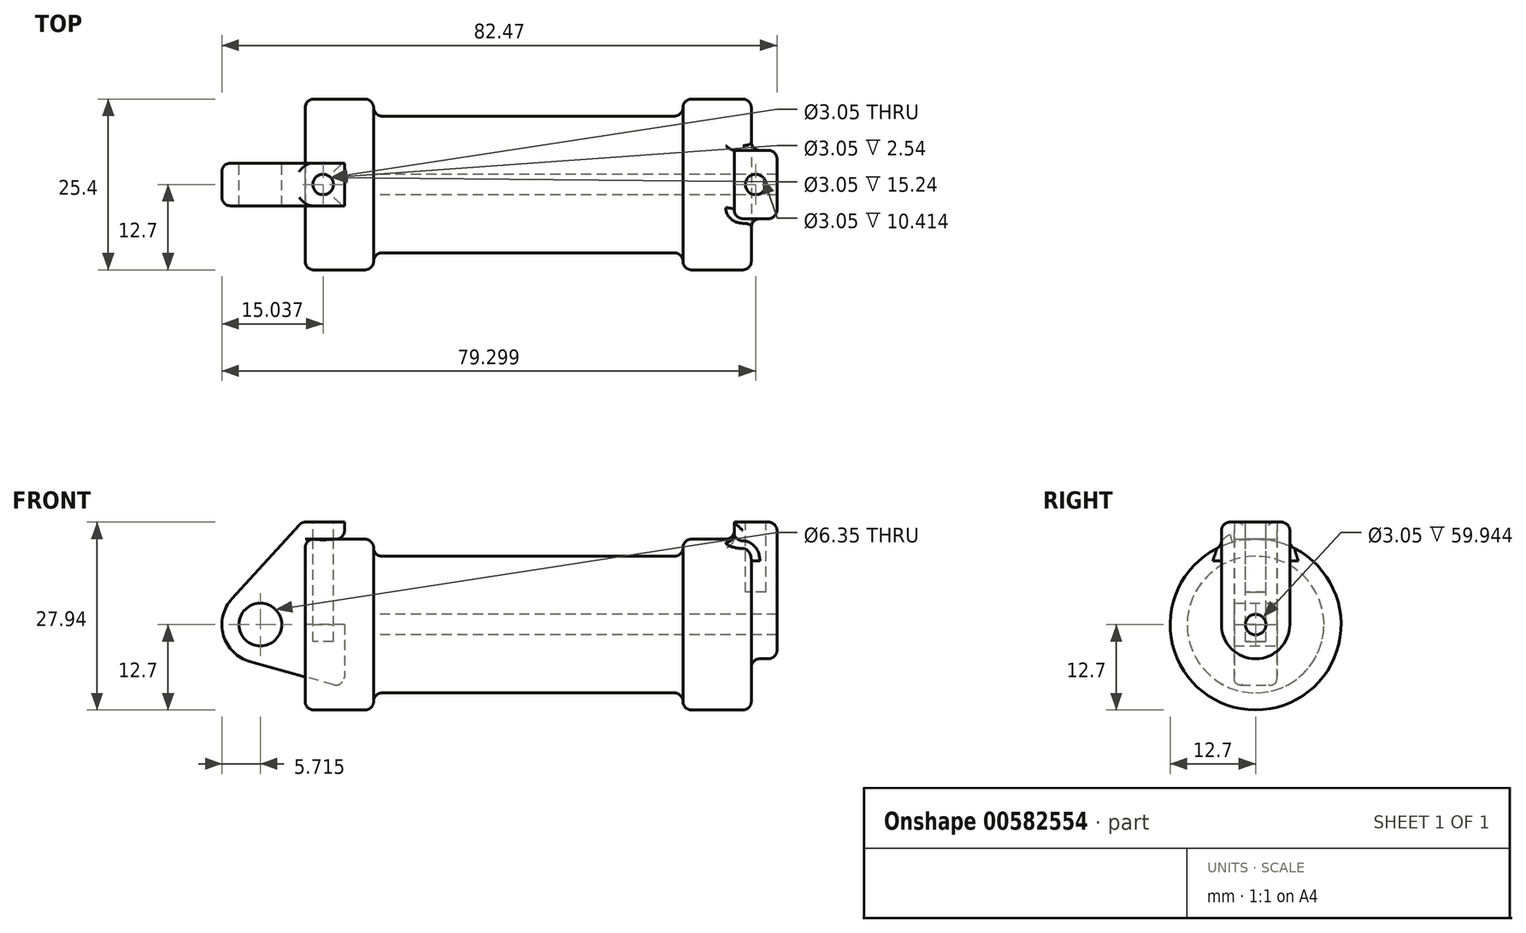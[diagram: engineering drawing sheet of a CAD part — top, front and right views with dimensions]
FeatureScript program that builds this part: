
annotation { "Feature Type Name" : "Feature", "Feature Type Description" : "" }
export const myFeature = defineFeature(function(context is Context, id is Id, definition is map)
    precondition{}
    {
        {
            var Q0;
            Q0=qCreatedBy(makeId("Front.planeOp"),FACE);
            var sketch = newSketch(context, id + "F0", { "sketchPlane" : qUnion([Q0])});
            skLineSegment(sketch, "E0", {"start": v(0, 0) * mm, "end": v(0, 12.7) * mm});
            skLineSegment(sketch, "E1", {"start": v(0, 12.7) * mm, "end": v(10.16, 12.7) * mm});
            skLineSegment(sketch, "E2", {"start": v(10.16, 12.7) * mm, "end": v(10.16, 10.16) * mm});
            skLineSegment(sketch, "E3", {"start": v(10.16, 10.16) * mm, "end": v(56.13, 10.16) * mm});
            skLineSegment(sketch, "E4", {"start": v(56.13, 10.16) * mm, "end": v(56.13, 12.7) * mm});
            skLineSegment(sketch, "E5", {"start": v(56.13, 12.7) * mm, "end": v(66.3, 12.7) * mm});
            skLineSegment(sketch, "E6", {"start": v(66.3, 12.7) * mm, "end": v(66.3, 0) * mm});
            skLineSegment(sketch, "E7", {"start": v(66.3, 0) * mm, "end": v(0, 0) * mm});
            skLineSegment(sketch, "E8", {"start": v(5.84, 15.24) * mm, "end": v(-0.5, 15.24) * mm});
            skLineSegment(sketch, "E9", {"start": v(-0.5, 15.24) * mm, "end": v(-10.88, 3.85) * mm});
            skLineSegment(sketch, "E10", {"start": v(0, 0) * mm, "end": v(-6.65, 0) * mm});
            skCircle(sketch, "E11", {"center": v(-6.65, 0) * mm, "radius": 5.72 * mm});
            skCircle(sketch, "E12", {"center": v(-6.65, 0) * mm, "radius": 3.18 * mm});
            skLineSegment(sketch, "E13", {"start": v(5.84, 15.24) * mm, "end": v(5.84, -9.4) * mm});
            skLineSegment(sketch, "E14", {"start": v(5.84, -9.4) * mm, "end": v(-8.18, -5.5) * mm});
            skSolve(sketch);
        }
        {
            var Q0;
            {var subQ0=sQuery(id+"F0.wireOp",EDGE,"E2");Q0=makeQuery(id+"F0.imprint","IMPRINT",FACE,{"disambiguationData":[TD([[makeQuery(id+"F0.imprint","IMPRINT",EDGE,{"derivedFrom":subQ0}),-1.0]])]});}
            var Q1;
            {var subQ0=sQuery(id+"F0.wireOp",EDGE,"E0");Q1=makeQuery(id+"F0.imprint","IMPRINT",FACE,{"disambiguationData":[TD([[makeQuery(id+"F0.imprint","IMPRINT",EDGE,{"derivedFrom":subQ0}),-1.0]])]});}
            var Q2;
            Q2=sQuery(id+"F0.wireOp",EDGE,"E7");
            revolve(context, id + "F1", {"entities" : qUnion([Q0, Q1]), "axis" : qUnion([Q2]), "revolveType" : RevolveType.FULL});
        }
        {
            var Q0;
            {var subQ1=sQuery(id+"F0.wireOp",EDGE,"E0");Q0=makeQuery(id+"F0.imprint","IMPRINT",FACE,{"disambiguationData":[TD([[makeQuery(id+"F0.imprint","IMPRINT",EDGE,{"derivedFrom":subQ1}),1.0]])]});}
            var Q1;
            {var subQ0=sQuery(id+"F0.wireOp",EDGE,"E14");Q1=makeQuery(id+"F0.imprint","IMPRINT",FACE,{"disambiguationData":[TD([[makeQuery(id+"F0.imprint","IMPRINT",EDGE,{"derivedFrom":subQ0}),-1.0]])]});}
            var Q2;
            {var subQ5=sQuery(id+"F0.wireOp",EDGE,"E12");Q2=makeQuery(id+"F0.imprint","IMPRINT",FACE,{"disambiguationData":[TD([[makeQuery(id+"F0.imprint","IMPRINT",EDGE,{"derivedFrom":subQ5}),-1.0]])]});}
            extrude(context, id + "F2", {"entities" : qUnion([Q0, Q1, Q2]), "endBound" : BoundingType.SYMMETRIC, "depth" : 6.35 * mm, "offsetDistance" : 25.4 * mm});
        }
        {
            var Q0;
            Q0=makeQuery(id+"F1.opRevolve","SWEPT_FACE",FACE,{"disambiguationData":[OSD([sQuery(id+"F0.wireOp",EDGE,"E6")])]});
            var sketch = newSketch(context, id + "F3", { "sketchPlane" : qUnion([Q0])});
            skCircle(sketch, "E15", {"center": v(0, 0) * mm, "radius": 1.52 * mm});
            skCircle(sketch, "E16", {"center": v(0, 0) * mm, "radius": 5.08 * mm});
            skLineSegment(sketch, "E17", {"start": v(5.08, 0) * mm, "end": v(5.08, 15.24) * mm});
            skLineSegment(sketch, "E18", {"start": v(-5.08, 0) * mm, "end": v(-5.08, 15.24) * mm});
            skLineSegment(sketch, "E19", {"start": v(5.08, 15.24) * mm, "end": v(-5.08, 15.24) * mm});
            skSolve(sketch);
        }
        {
            var Q0;
            Q0 = qSketchRegion(id + "F3", true);
            extrude(context, id + "F4", {"entities" : qUnion([Q0]), "operationType" : NewBodyOperationType.ADD, "endBound" : BoundingType.SYMMETRIC, "depth" : 7.62 * mm, "offsetDistance" : 25.4 * mm});
        }
        {
            var Q0;
            Q0=makeQuery(id+"F4.opExtrude","CAP_FACE",FACE,{"disambiguationData":[OSD([sQuery(id+"F3.wireOp",EDGE,"E15"),sQuery(id+"F3.wireOp",EDGE,"E16"),sQuery(id+"F3.wireOp",EDGE,"E17"),sQuery(id+"F3.wireOp",EDGE,"E18"),sQuery(id+"F3.wireOp",EDGE,"E19")])],"isStart":true});
            extrude(context, id + "F5", {"entities" : qUnion([Q0]), "operationType" : NewBodyOperationType.REMOVE, "oppositeDirection" : true, "depth" : 1.27 * mm, "offsetDistance" : 25.4 * mm});
        }
        {
            var Q0;
            Q0=makeQuery(id+"F4.boolean.opBoolean","SPLIT",FACE,{"disambiguationData":[TD([makeQuery(id+"F4.opExtrude","SWEPT_FACE",FACE,{"disambiguationData":[OSD([sQuery(id+"F3.wireOp",EDGE,"E15")])]})])],"derivedFrom":makeQuery(id+"F1.opRevolve","SWEPT_FACE",FACE,{"disambiguationData":[OSD([sQuery(id+"F0.wireOp",EDGE,"E6")])]})});
            var Q1;
            Q1=makeQuery(id+"F1.opRevolve","SWEPT_FACE",FACE,{"disambiguationData":[OSD([sQuery(id+"F0.wireOp",EDGE,"E2")])]});
            extrude(context, id + "F6", {"entities" : qUnion([Q0]), "operationType" : NewBodyOperationType.REMOVE, "endBound" : BoundingType.UP_TO_SURFACE, "oppositeDirection" : true, "depth" : 25.4 * mm, "endBoundEntityFace" : qUnion([Q1]), "offsetDistance" : 25.4 * mm});
        }
        {
            var Q0;
            Q0=makeQuery(id+"F2.opExtrude","SWEPT_FACE",FACE,{"disambiguationData":[OSD([sQuery(id+"F0.wireOp",EDGE,"E8")])]});
            var sketch = newSketch(context, id + "F7", { "sketchPlane" : qUnion([Q0])});
            skCircle(sketch, "E20", {"center": v(2.67, 0) * mm, "radius": 1.52 * mm});
            skSolve(sketch);
        }
        {
            var Q0;
            Q0=makeQuery(id+"F4.opExtrude","SWEPT_FACE",FACE,{"disambiguationData":[OSD([sQuery(id+"F3.wireOp",EDGE,"E19")])]});
            var sketch = newSketch(context, id + "F8", { "sketchPlane" : qUnion([Q0])});
            skCircle(sketch, "E21", {"center": v(66.93, 0) * mm, "radius": 1.52 * mm});
            skLineSegment(sketch, "E22", {"start": v(63.75, 0) * mm, "end": v(70.1, 0) * mm, "construction": true});
            skSolve(sketch);
        }
        {
            var Q0;
            Q0 = qSketchRegion(id + "F7", true);
            extrude(context, id + "F9", {"entities" : qUnion([Q0]), "operationType" : NewBodyOperationType.REMOVE, "oppositeDirection" : true, "depth" : 17.78 * mm, "offsetDistance" : 25.4 * mm});
        }
        {
            var Q0;
            Q0=makeQuery(id+"F8.imprint","IMPRINT",FACE,{"disambiguationData":[TD([[makeQuery(id+"F8.imprint","IMPRINT",EDGE,{"derivedFrom":sQuery(id+"F8.wireOp",EDGE,"E21")}),1.0]])]});
            extrude(context, id + "F10", {"entities" : qUnion([Q0]), "operationType" : NewBodyOperationType.REMOVE, "oppositeDirection" : true, "depth" : 10.4 * mm, "offsetDistance" : 25.4 * mm});
        }
        {
            var Q0;
            Q0=makeQuery(id+"F4.boolean.opBoolean","SPLIT",FACE,{"disambiguationData":[TD([makeQuery(id+"F1.opRevolve","SWEPT_FACE",FACE,{"disambiguationData":[OSD([sQuery(id+"F0.wireOp",EDGE,"E5")])]})])],"derivedFrom":makeQuery(id+"F1.opRevolve","SWEPT_FACE",FACE,{"disambiguationData":[OSD([sQuery(id+"F0.wireOp",EDGE,"E6")])]})});
            var Q1;
            Q1=makeQuery(id+"F4.opExtrude","CAP_EDGE",EDGE,{"disambiguationData":[OSD([sQuery(id+"F3.wireOp",EDGE,"E17")])],"isStart":false});
            var Q2;
            Q2=makeQuery(id+"F4.opExtrude","CAP_EDGE",EDGE,{"disambiguationData":[OSD([sQuery(id+"F3.wireOp",EDGE,"E16")])],"isStart":false});
            var Q3;
            Q3=makeQuery(id+"F4.opExtrude","SWEPT_FACE",FACE,{"disambiguationData":[OSD([sQuery(id+"F3.wireOp",EDGE,"E18")])]});
            var Q4;
            {var subQ0=sQuery(id+"F0.wireOp",EDGE,"E5");Q4=makeQuery(id+"F5.boolean.opBoolean","MERGE",FACE,{"derivedFrom":[makeQuery(id+"F1.opRevolve","SWEPT_FACE",FACE,{"disambiguationData":[OSD([subQ0])]}),makeQuery(id+"F5.opExtrude","SWEPT_FACE",FACE,{"disambiguationData":[OSD([subQ0,sQuery(id+"F3.wireOp",EDGE,"E15"),sQuery(id+"F3.wireOp",EDGE,"E16"),sQuery(id+"F3.wireOp",EDGE,"E17"),sQuery(id+"F3.wireOp",EDGE,"E18"),sQuery(id+"F3.wireOp",EDGE,"E19")])]})]});}
            var Q5;
            Q5=makeQuery(id+"F1.opRevolve","SWEPT_EDGE",EDGE,{"disambiguationData":[OSD([sQuery(id+"F0.wireOp",EDGE,"E4"),sQuery(id+"F0.wireOp",EDGE,"E5")])]});
            var Q6;
            Q6=makeQuery(id+"F1.opRevolve","SWEPT_EDGE",EDGE,{"disambiguationData":[OSD([sQuery(id+"F0.wireOp",EDGE,"E3"),sQuery(id+"F0.wireOp",EDGE,"E4")])]});
            var Q7;
            Q7=makeQuery(id+"F1.opRevolve","SWEPT_FACE",FACE,{"disambiguationData":[OSD([sQuery(id+"F0.wireOp",EDGE,"E3")])]});
            var Q8;
            Q8=makeQuery(id+"F1.opRevolve","SWEPT_EDGE",EDGE,{"disambiguationData":[OSD([sQuery(id+"F0.wireOp",EDGE,"E1"),sQuery(id+"F0.wireOp",EDGE,"E2")])]});
            var Q9;
            Q9=makeQuery(id+"F1.opRevolve","SWEPT_EDGE",EDGE,{"disambiguationData":[OSD([sQuery(id+"F0.wireOp",EDGE,"E2"),sQuery(id+"F0.wireOp",EDGE,"E3")])]});
            var Q10;
            Q10=makeQuery(id+"F2.opExtrude","SWEPT_FACE",FACE,{"disambiguationData":[OSD([sQuery(id+"F0.wireOp",EDGE,"E9")])]});
            var Q11;
            Q11=makeQuery(id+"F2.opExtrude","SWEPT_FACE",FACE,{"disambiguationData":[OSD([sQuery(id+"F0.wireOp",EDGE,"E14")])]});
            var Q12;
            Q12=makeQuery(id+"F2.opExtrude","SWEPT_FACE",FACE,{"disambiguationData":[OSD([sQuery(id+"F0.wireOp",EDGE,"E11")])]});
            var Q13;
            Q13=makeQuery(id+"F2.opExtrude","SWEPT_EDGE",EDGE,{"disambiguationData":[OSD([sQuery(id+"F0.wireOp",EDGE,"E1"),sQuery(id+"F0.wireOp",EDGE,"E13")])]});
            var Q14;
            Q14=makeQuery(id+"F1.opRevolve","SWEPT_FACE",FACE,{"disambiguationData":[OSD([sQuery(id+"F0.wireOp",EDGE,"E0")])]});
            var Q15;
            Q15=makeQuery(id+"F5.boolean.opBoolean","COPY",EDGE,{"derivedFrom":makeQuery(id+"F5.opExtrude","CAP_EDGE",EDGE,{"disambiguationData":[OSD([sQuery(id+"F3.wireOp",EDGE,"E19")])],"isStart":false})});
            var Q16;
            Q16=makeQuery(id+"F4.opExtrude","SWEPT_EDGE",EDGE,{"disambiguationData":[OSD([sQuery(id+"F3.wireOp",EDGE,"E17"),sQuery(id+"F3.wireOp",EDGE,"E19")])]});
            var Q17;
            Q17=makeQuery(id+"F5.boolean.opBoolean","COPY",EDGE,{"derivedFrom":makeQuery(id+"F5.opExtrude","CAP_EDGE",EDGE,{"disambiguationData":[OSD([sQuery(id+"F3.wireOp",EDGE,"E17")])],"isStart":false})});
            var Q18;
            Q18=makeQuery(id+"F4.opExtrude","CAP_EDGE",EDGE,{"disambiguationData":[OSD([sQuery(id+"F3.wireOp",EDGE,"E19")])],"isStart":false});
            fillet(context, id + "F11", {"entities" : qUnion([Q0, Q1, Q2, Q3, Q4, Q5, Q6, Q7, Q8, Q9, Q10, Q11, Q12, Q13, Q14, Q15, Q16, Q17, Q18]), "radius" : 1.27 * mm, "tangentPropagation" : true, "allowEdgeOverflow" : false});
        }
    });
